# Revit family: Storage-Teknion-EMC1_Low_Single_Cabinet-R2016
name_source: partatom
category: Furniture
revit_build: Autodesk Revit 2018 (Build: 20190510_1515(x64)
units: mm (PartAtom-declared; Revit-internal decimal feet)

## family parameters
Always vertical = Yes
Cut with Voids When Loaded = No
OmniClass Number = 23.40.20.00
OmniClass Title = General Furniture and Specialties
Room Calculation Point = No
Shared = Yes
Work Plane-Based = No

## types (4) — shared parameters
Assembly Code = E2020200
Manufacturer = Teknion
Manufacturer Fax = 416.661.4586
Part Number = EMC1
Product Documentation Link = https://assets.teknion.com
Product Line = Emote
Product Page URL = https://www.teknion.com
Series = Emote
Sustainability Data = https://www.teknion.com
URL = www.teknion.com
Unit Weight URL = http://www.teknion.com
Warranty = http://www.teknion.com

## per-type parameters (varying)
| type | Description | Double Doors | Full Height Drawer | Model | Open | Partial Height Drawer | Single Door |
| Open Drawer Configuration | Low Single Cabinet, Open Drawer Configuration , 29" Width | No | No | EMC1OP29 | Yes | No | No |
| Double Doors Drawer Configuration | Low Single Cabinet, Double Doors Drawer Configuration , 29" Width | Yes | No | EMC1CL29 | No | No | No |
| Partial Height Drawer Configuration | Low Single Cabinet, Partial Height Drawer Configuration , 29" Width | No | No | EMC1PD29 | No | Yes | Yes |
| Full Height Drawer Configuration | Low Single Cabinet, Full Height Drawer Configuration , 29" Width | No | Yes | EMC1FD29 | No | No | Yes |

## geometry (parser evidence)
native form markers: Blend x41, Sweep x2
no freeform markers — native parametric forms only
